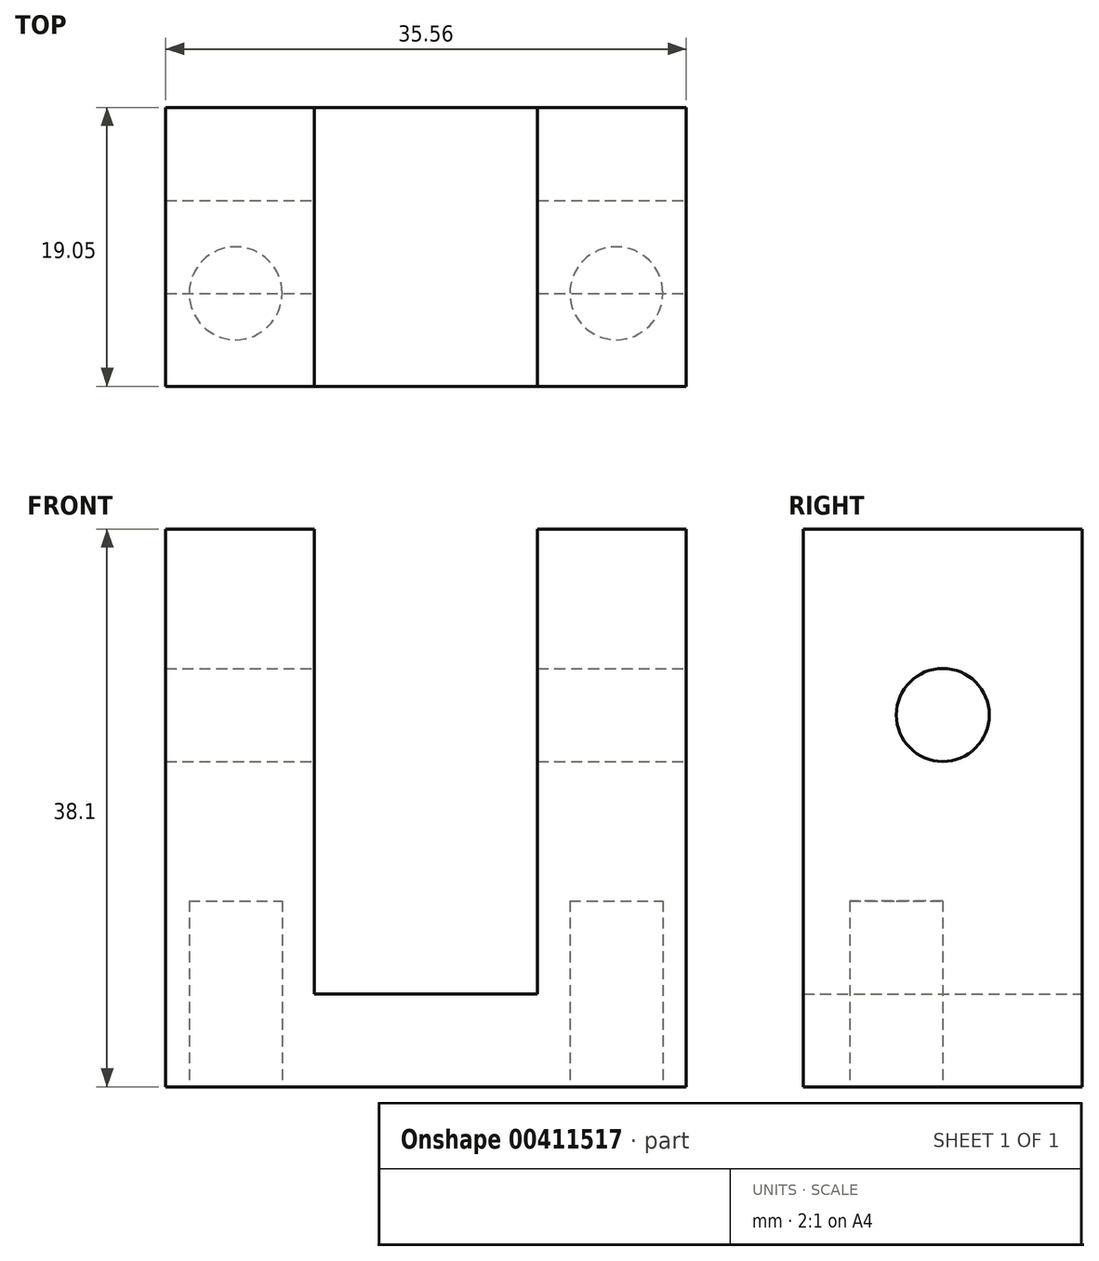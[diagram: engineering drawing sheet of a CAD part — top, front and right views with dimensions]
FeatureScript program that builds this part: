
annotation { "Feature Type Name" : "Feature", "Feature Type Description" : "" }
export const myFeature = defineFeature(function(context is Context, id is Id, definition is map)
    precondition{}
    {
        {
            var Q0;
            Q0=qCreatedBy(makeId("Front.planeOp"),FACE);
            var sketch = newSketch(context, id + "F0", { "sketchPlane" : qUnion([Q0])});
            skLineSegment(sketch, "E0", {"start": v(0, 0) * mm, "end": v(0, 38.1) * mm});
            skLineSegment(sketch, "E1", {"start": v(0, 38.1) * mm, "end": v(10.16, 38.1) * mm});
            skLineSegment(sketch, "E2", {"start": v(10.16, 38.1) * mm, "end": v(10.16, 6.35) * mm});
            skLineSegment(sketch, "E3", {"start": v(10.16, 6.35) * mm, "end": v(25.4, 6.35) * mm});
            skLineSegment(sketch, "E4", {"start": v(25.4, 6.35) * mm, "end": v(25.4, 38.1) * mm});
            skLineSegment(sketch, "E5", {"start": v(25.4, 38.1) * mm, "end": v(35.56, 38.1) * mm});
            skLineSegment(sketch, "E6", {"start": v(35.56, 38.1) * mm, "end": v(35.56, 0) * mm});
            skLineSegment(sketch, "E7", {"start": v(35.56, 0) * mm, "end": v(0, 0) * mm});
            skSolve(sketch);
        }
        {
            var Q0;
            Q0=makeQuery(id+"F0.imprint","IMPRINT",FACE,{"disambiguationData":[TD([[makeQuery(id+"F0.imprint","IMPRINT",EDGE,{"derivedFrom":sQuery(id+"F0.wireOp",EDGE,"E0")}),-1.0]])]});
            extrude(context, id + "F1", {"entities" : qUnion([Q0]), "depth" : 19.05 * mm});
        }
        {
            var Q0;
            Q0=makeQuery(id+"F1.opExtrude","SWEPT_FACE",FACE,{"disambiguationData":[OSD([sQuery(id+"F0.wireOp",EDGE,"E6")])]});
            var sketch = newSketch(context, id + "F2", { "sketchPlane" : qUnion([Q0])});
            skCircle(sketch, "E8", {"center": v(-9.53, 25.4) * mm, "radius": 3.18 * mm});
            skSolve(sketch);
        }
        {
            var Q0;
            Q0=makeQuery(id+"F2.imprint","IMPRINT",FACE,{"disambiguationData":[TD([[makeQuery(id+"F2.imprint","IMPRINT",EDGE,{"derivedFrom":sQuery(id+"F2.wireOp",EDGE,"E8")}),1.0]])]});
            extrude(context, id + "F3", {"entities" : qUnion([Q0]), "operationType" : NewBodyOperationType.REMOVE, "oppositeDirection" : true, "depth" : 47 * mm});
        }
        {
            var Q0;
            Q0=makeQuery(id+"F1.opExtrude","SWEPT_FACE",FACE,{"disambiguationData":[OSD([sQuery(id+"F0.wireOp",EDGE,"E7")])]});
            var sketch = newSketch(context, id + "F4", { "sketchPlane" : qUnion([Q0])});
            skCircle(sketch, "E9", {"center": v(30.78, 12.7) * mm, "radius": 3.17 * mm});
            skCircle(sketch, "E10", {"center": v(4.78, 12.7) * mm, "radius": 3.18 * mm});
            skSolve(sketch);
        }
        {
            var Q0;
            Q0 = qSketchRegion(id + "F4", true);
            extrude(context, id + "F5", {"entities" : qUnion([Q0]), "operationType" : NewBodyOperationType.REMOVE, "oppositeDirection" : true, "depth" : 12.7 * mm});
        }
    });
